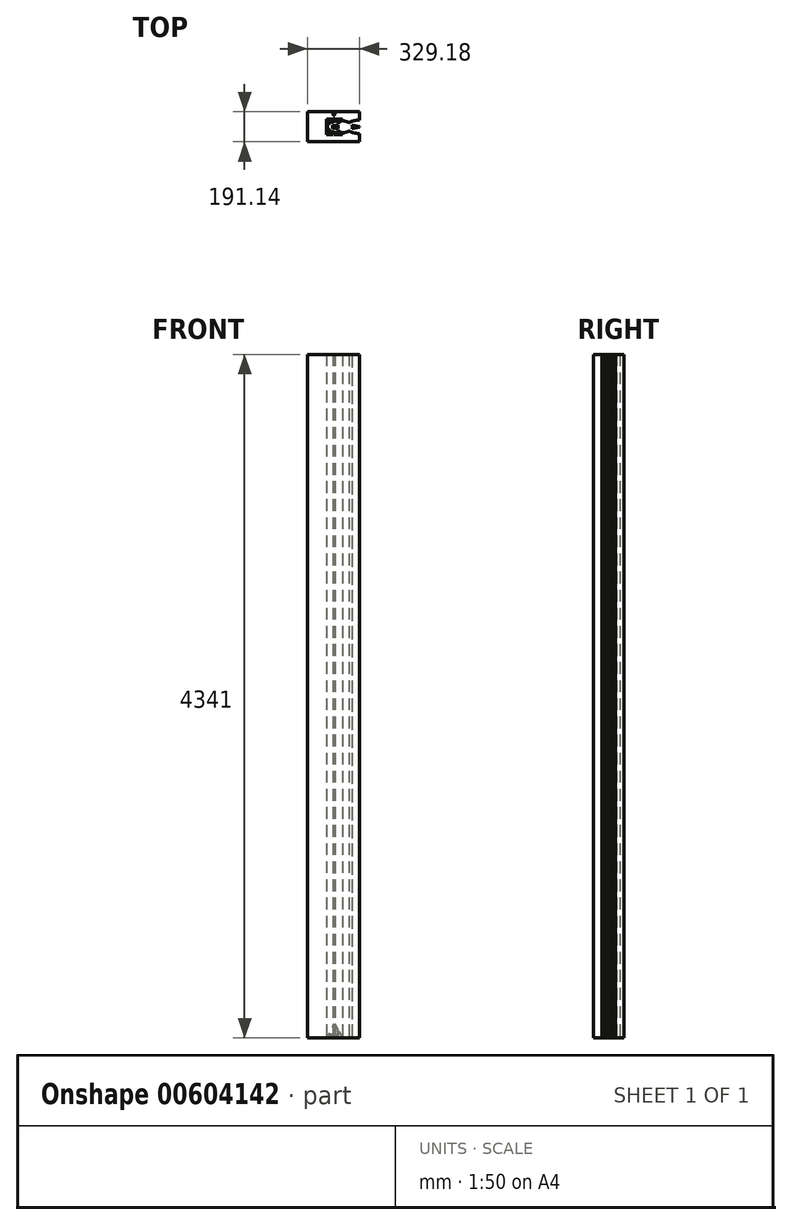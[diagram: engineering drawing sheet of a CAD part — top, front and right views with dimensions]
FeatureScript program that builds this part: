
annotation { "Feature Type Name" : "Feature", "Feature Type Description" : "" }
export const myFeature = defineFeature(function(context is Context, id is Id, definition is map)
    precondition{}
    {
        {
            var Q0;
            Q0=qCreatedBy(makeId("Top.planeOp"),FACE);
            var sketch = newSketch(context, id + "F0", { "sketchPlane" : qUnion([Q0])});
            skLineSegment(sketch, "E0.bottom", {"start": v(55.2, -50) * mm, "end": v(-44.8, -50) * mm});
            skLineSegment(sketch, "E0.top", {"start": v(55.2, 50) * mm, "end": v(-44.8, 50) * mm});
            skLineSegment(sketch, "E0.left", {"start": v(55.2, -50) * mm, "end": v(55.2, 50) * mm});
            skLineSegment(sketch, "E0.right", {"start": v(-44.8, -50) * mm, "end": v(-44.8, 50) * mm});
            skPoint(sketch, "E0.middle", {"position": v(5.2, 0) * mm});
            skSolve(sketch);
        }
        {
            var Q0;
            Q0=makeQuery(id+"F0.imprint","IMPRINT",FACE,{"disambiguationData":[TD([[makeQuery(id+"F0.imprint","IMPRINT",EDGE,{"derivedFrom":sQuery(id+"F0.wireOp",EDGE,"E0.bottom")}),-1.0]])]});
            extrude(context, id + "F1", {"entities" : qUnion([Q0]), "depth" : 90 * mm, "offsetDistance" : 25 * mm});
        }
        {
            var Q0;
            Q0=makeQuery(id+"F1.opExtrude","CAP_EDGE",EDGE,{"disambiguationData":[OSD([sQuery(id+"F0.wireOp",EDGE,"E0.right")])],"isStart":false});
            chamfer(context, id + "F2", {"entities" : qUnion([Q0]), "chamferType" : ChamferType.TWO_OFFSETS, "width1" : 90 * mm, "oppositeDirection" : false, "width2" : 50 * mm, "tangentPropagation" : true});
        }
        {
            var Q0;
            Q0=makeQuery(id+"F1.opExtrude","CAP_EDGE",EDGE,{"disambiguationData":[OSD([sQuery(id+"F0.wireOp",EDGE,"E0.bottom")])],"isStart":false});
            chamfer(context, id + "F3", {"entities" : qUnion([Q0]), "chamferType" : ChamferType.TWO_OFFSETS, "width1" : 90 * mm, "oppositeDirection" : false, "width2" : 50 * mm, "tangentPropagation" : true});
        }
        {
            var Q0;
            Q0=makeQuery(id+"F1.opExtrude","CAP_EDGE",EDGE,{"disambiguationData":[OSD([sQuery(id+"F0.wireOp",EDGE,"E0.left")])],"isStart":false});
            chamfer(context, id + "F4", {"entities" : qUnion([Q0]), "chamferType" : ChamferType.TWO_OFFSETS, "width1" : 50 * mm, "oppositeDirection" : false, "width2" : 90 * mm, "tangentPropagation" : true});
        }
        {
            var Q0;
            Q0=qCreatedBy(makeId("Right.planeOp"),FACE);
            var sketch = newSketch(context, id + "F5", { "sketchPlane" : qUnion([Q0])});
            skLineSegment(sketch, "E1", {"start": v(0, 90) * mm, "end": v(50, 0) * mm});
            skLineSegment(sketch, "E2", {"start": v(0, 90) * mm, "end": v(50, 90) * mm});
            skLineSegment(sketch, "E3", {"start": v(50, 90) * mm, "end": v(50, 0) * mm});
            skSolve(sketch);
        }
        {
            var Q0;
            Q0 = qSketchRegion(id + "F5", true);
            extrude(context, id + "F6", {"entities" : qUnion([Q0]), "operationType" : NewBodyOperationType.REMOVE, "oppositeDirection" : true, "depth" : 50 * mm, "offsetDistance" : 25 * mm, "hasSecondDirection" : true, "secondDirectionOppositeDirection" : false, "secondDirectionDepth" : 50 * mm});
        }
        {
            var Q0;
            Q0=makeQuery(id+"F6.boolean.opBoolean","COPY",FACE,{"derivedFrom":makeQuery(id+"F6.opExtrude","CAP_FACE",FACE,{"disambiguationData":[OSD([sQuery(id+"F5.wireOp",EDGE,"E1"),sQuery(id+"F5.wireOp",EDGE,"E2"),sQuery(id+"F5.wireOp",EDGE,"E3")])],"isStart":true})});
            extrude(context, id + "F7", {"entities" : qUnion([Q0]), "operationType" : NewBodyOperationType.REMOVE, "oppositeDirection" : true, "depth" : 25 * mm, "offsetDistance" : 25 * mm});
        }
        {
            var Q0;
            Q0=qCreatedBy(makeId("Top.planeOp"),FACE);
            var sketch = newSketch(context, id + "F8", { "sketchPlane" : qUnion([Q0])});
            skLineSegment(sketch, "E4.bottom", {"start": v(164.6, 95.57) * mm, "end": v(-164.6, 95.57) * mm});
            skLineSegment(sketch, "E4.top", {"start": v(164.6, -95.57) * mm, "end": v(-164.6, -95.57) * mm});
            skLineSegment(sketch, "E4.left", {"start": v(164.6, 95.57) * mm, "end": v(164.6, -95.57) * mm});
            skLineSegment(sketch, "E4.right", {"start": v(-164.6, 95.57) * mm, "end": v(-164.6, -95.57) * mm});
            skPoint(sketch, "E4.middle", {"position": v(0, 0) * mm});
            skSolve(sketch);
        }
        {
            var Q0;
            Q0=makeQuery(id+"F8.imprint","IMPRINT",FACE,{"disambiguationData":[TD([[makeQuery(id+"F8.imprint","IMPRINT",EDGE,{"derivedFrom":sQuery(id+"F8.wireOp",EDGE,"E4.bottom")}),1.0]])]});
            extrude(context, id + "F9", {"entities" : qUnion([Q0]), "operationType" : NewBodyOperationType.ADD, "oppositeDirection" : true, "depth" : 1 * mm, "offsetDistance" : 25 * mm});
        }
        {
            var Q0;
            Q0=qCreatedBy(makeId("Front.planeOp"),FACE);
            var sketch = newSketch(context, id + "F10", { "sketchPlane" : qUnion([Q0])});
            skLineSegment(sketch, "E5.bottom", {"start": v(-2.3, 7) * mm, "end": v(2.7, 7) * mm});
            skLineSegment(sketch, "E5.top", {"start": v(-2.3, 0) * mm, "end": v(2.7, 0) * mm});
            skLineSegment(sketch, "E5.left", {"start": v(-2.3, 7) * mm, "end": v(-2.3, 0) * mm});
            skLineSegment(sketch, "E5.right", {"start": v(2.7, 7) * mm, "end": v(2.7, 0) * mm});
            skSolve(sketch);
        }
        {
            var Q0;
            Q0 = qSketchRegion(id + "F10", true);
            extrude(context, id + "F11", {"entities" : qUnion([Q0]), "operationType" : NewBodyOperationType.REMOVE, "depth" : 100 * mm, "offsetDistance" : 25 * mm});
        }
        {
            var Q0;
            Q0=makeQuery(id+"F3.opChamfer","BLEND_FACE",FACE,{"disambiguationData":[OSD([sQuery(id+"F0.wireOp",EDGE,"E0.bottom")])]});
            var sketch = newSketch(context, id + "F12", { "sketchPlane" : qUnion([Q0])});
            skText(sketch, "E6", { "text": "James", "fontName": "OpenSans-Regular.ttf"});
            const initialGuessF12  = {"E6": [-0.02696, -0.00383, 1, 0, 0.01599]};
            skSetInitialGuess(sketch, initialGuessF12);
            skSolve(sketch);
        }
        {
            var Q0;
            Q0 = qSketchRegion(id + "F12", true);
            extrude(context, id + "F13", {"entities" : qUnion([Q0]), "operationType" : NewBodyOperationType.REMOVE, "oppositeDirection" : true, "depth" : 9999 * mm, "offsetDistance" : 25 * mm});
        }
        {
            var Q0;
            Q0=makeQuery(id+"F13.boolean.opBoolean","SPLIT",FACE,{"disambiguationData":[TD([makeQuery(id+"F2.opChamfer","BLEND_FACE",FACE,{"disambiguationData":[OSD([sQuery(id+"F0.wireOp",EDGE,"E0.right")])]})])],"derivedFrom":makeQuery(id+"F3.opChamfer","BLEND_FACE",FACE,{"disambiguationData":[OSD([sQuery(id+"F0.wireOp",EDGE,"E0.bottom")])]})});
            var sketch = newSketch(context, id + "F14", { "sketchPlane" : qUnion([Q0])});
            skCircle(sketch, "E7", {"center": v(2.1, 40.18) * mm, "radius": 5.75 * mm});
            skSolve(sketch);
        }
        {
            var Q0;
            Q0=makeQuery(id+"F14.imprint","IMPRINT",FACE,{"disambiguationData":[TD([[makeQuery(id+"F14.imprint","IMPRINT",EDGE,{"derivedFrom":sQuery(id+"F14.wireOp",EDGE,"E7")}),1.0]])]});
            extrude(context, id + "F15", {"entities" : qUnion([Q0]), "operationType" : NewBodyOperationType.REMOVE, "oppositeDirection" : true, "depth" : 999 * mm, "offsetDistance" : 25 * mm});
        }
        {
            var Q0;
            {var subQ0=sQuery(id+"F8.wireOp",EDGE,"E4.left");var subQ1=sQuery(id+"F8.wireOp",EDGE,"E4.top");var subQ2=sQuery(id+"F8.wireOp",EDGE,"E4.right");var subQ3=sQuery(id+"F8.wireOp",EDGE,"E4.bottom");Q0=makeQuery(id+"F13.boolean.opBoolean","SPLIT",FACE,{"disambiguationData":[TD([makeQuery(id+"F9.opExtrude","SWEPT_FACE",FACE,{"disambiguationData":[OSD([subQ3])]})])],"derivedFrom":makeQuery(id+"F9.opExtrude","CAP_FACE",FACE,{"disambiguationData":[OSD([subQ3,subQ1,subQ0,subQ2])],"isStart":false})});}
            var sketch = newSketch(context, id + "F16", { "sketchPlane" : qUnion([Q0])});
            skCircle(sketch, "E8", {"center": v(0, 0) * mm, "radius": 18.47 * mm});
            skSolve(sketch);
        }
        {
            var Q0;
            Q0 = qSketchRegion(id + "F16", true);
            extrude(context, id + "F17", {"entities" : qUnion([Q0]), "operationType" : NewBodyOperationType.REMOVE, "oppositeDirection" : true, "depth" : 67 * mm, "offsetDistance" : 25 * mm});
        }
        {
            var Q0;
            Q0=makeQuery(id+"F2.opChamfer","BLEND_FACE",FACE,{"disambiguationData":[OSD([sQuery(id+"F0.wireOp",EDGE,"E0.right")])]});
            var sketch = newSketch(context, id + "F18", { "sketchPlane" : qUnion([Q0])});
            skCircle(sketch, "E9", {"center": v(0, 81.2) * mm, "radius": 42.91 * mm});
            skSolve(sketch);
        }
        {
            var Q0;
            {var subQ0=sQuery(id+"F18.wireOp",EDGE,"E9");var subQ1=makeQuery(id+"F2.opChamfer","BLEND_FACE",FACE,{"disambiguationData":[OSD([sQuery(id+"F0.wireOp",EDGE,"E0.right")])]});var subQ2=makeQuery(id+"F3.opChamfer","BLEND_EDGE",EDGE,{"blendedFrom":[makeQuery(id+"F1.opExtrude","CAP_EDGE",EDGE,{"disambiguationData":[OSD([sQuery(id+"F0.wireOp",EDGE,"E0.bottom")])],"isStart":false}),subQ1],"blendedInto":[subQ1]});var subQ3=makeQuery(id+"F18.imprint","INTERSECT",VERTEX,{"derivedFrom":[subQ2,subQ0]});Q0=makeQuery(id+"F18.imprint","IMPRINT",FACE,{"disambiguationData":[TD([[makeQuery(id+"F18.imprint","IMPRINT",EDGE,{"disambiguationData":[TD([[subQ3,-1.0]])],"derivedFrom":subQ0}),1.0]])]});}
            extrude(context, id + "F19", {"entities" : qUnion([Q0]), "operationType" : NewBodyOperationType.REMOVE, "oppositeDirection" : true, "depth" : 9999 * mm, "offsetDistance" : 25 * mm});
        }
        {
            var Q0;
            Q0=makeQuery(id+"F2.opChamfer","BLEND_FACE",FACE,{"disambiguationData":[OSD([sQuery(id+"F0.wireOp",EDGE,"E0.right")])]});
            var sketch = newSketch(context, id + "F20", { "sketchPlane" : qUnion([Q0])});
            skCircle(sketch, "E10", {"center": v(0, 19) * mm, "radius": 39.27 * mm});
            skSolve(sketch);
        }
        {
            var Q0;
            {var subQ0=sQuery(id+"F20.wireOp",EDGE,"E10");var subQ1=sQuery(id+"F5.wireOp",EDGE,"E1");var subQ2=sQuery(id+"F0.wireOp",EDGE,"E0.right");var subQ3=makeQuery(id+"F6.boolean.opBoolean","INTERSECT",EDGE,{"derivedFrom":[makeQuery(id+"F2.opChamfer","BLEND_FACE",FACE,{"disambiguationData":[OSD([subQ2])]}),makeQuery(id+"F6.opExtrude","SWEPT_FACE",FACE,{"disambiguationData":[OSD([subQ1])]})]});var subQ6=makeQuery(id+"F19.boolean.opBoolean","SPLIT",EDGE,{"derivedFrom":subQ3});var subQ7=makeQuery(id+"F20.imprint","INTERSECT",VERTEX,{"derivedFrom":[subQ6,subQ0]});Q0=makeQuery(id+"F20.imprint","IMPRINT",FACE,{"disambiguationData":[TD([[makeQuery(id+"F20.imprint","IMPRINT",EDGE,{"disambiguationData":[TD([[subQ7,1.0]])],"derivedFrom":subQ0}),1.0]])]});}
            var Q1;
            {var subQ0=sQuery(id+"F5.wireOp",EDGE,"E1");var subQ1=sQuery(id+"F0.wireOp",EDGE,"E0.right");var subQ2=makeQuery(id+"F2.opChamfer","BLEND_FACE",FACE,{"disambiguationData":[OSD([subQ1])]});var subQ3=makeQuery(id+"F6.boolean.opBoolean","INTERSECT",EDGE,{"derivedFrom":[subQ2,makeQuery(id+"F6.opExtrude","SWEPT_FACE",FACE,{"disambiguationData":[OSD([subQ0])]})]});var subQ4=makeQuery(id+"F19.boolean.opBoolean","SPLIT",EDGE,{"derivedFrom":subQ3});var subQ7=sQuery(id+"F20.wireOp",EDGE,"E10");var subQ15=makeQuery(id+"F20.imprint","INTERSECT",VERTEX,{"derivedFrom":[subQ4,subQ7]});Q1=makeQuery(id+"F20.imprint","IMPRINT",FACE,{"disambiguationData":[TD([[makeQuery(id+"F20.imprint","IMPRINT",EDGE,{"disambiguationData":[TD([[subQ15,-1.0]])],"derivedFrom":subQ7}),1.0]])]});}
            extrude(context, id + "F21", {"entities" : qUnion([Q0, Q1]), "operationType" : NewBodyOperationType.REMOVE, "oppositeDirection" : true, "depth" : 9909 * mm, "offsetDistance" : 25 * mm});
        }
        {
            var Q0;
            {var subQ1=sQuery(id+"F8.wireOp",EDGE,"E4.right");var subQ2=sQuery(id+"F8.wireOp",EDGE,"E4.top");var subQ3=sQuery(id+"F8.wireOp",EDGE,"E4.bottom");var subQ5=sQuery(id+"F8.wireOp",EDGE,"E4.left");var subQ6=makeQuery(id+"F9.opExtrude","CAP_FACE",FACE,{"disambiguationData":[OSD([subQ3,subQ2,subQ5,subQ1])],"isStart":true});var subQ8=makeQuery(id+"F11.opExtrude","SWEPT_FACE",FACE,{"disambiguationData":[OSD([sQuery(id+"F10.wireOp",EDGE,"E5.top")])]});var subQ10=sQuery(id+"F0.wireOp",EDGE,"E0.right");Q0=makeQuery(id+"F21.boolean.opBoolean","SPLIT",FACE,{"disambiguationData":[TD([makeQuery(id+"F2.opChamfer","BLEND_FACE",FACE,{"disambiguationData":[OSD([subQ10])]})])],"derivedFrom":makeQuery(id+"F11.boolean.opBoolean","MERGE",FACE,{"derivedFrom":[subQ6,subQ8]})});}
            extrude(context, id + "F22", {"entities" : qUnion([Q0]), "operationType" : NewBodyOperationType.ADD, "depth" : 4340 * mm, "offsetDistance" : 25 * mm});
        }
    });
